# Revit family: MKH1-800-R3(R4)
name_source: partatom
category: Mechanical Equipment
revit_build: Autodesk Revit 2013 (Build: 20120221_2030(x64)
units: mm (PartAtom-declared; Revit-internal decimal feet)

## types (2) — shared parameters
Circuit breaker = 15 A
Condensation = water
Depth = 1360 mm
Description = High efficiency water cooled
Drain pipe = 18.5 mm
Height = 200 mm
Installation = Indoor installation
Liquid pipe = 19.05 mm  [stored 0.0625 ft]
Machine material = Galvanized Steel
Manufacturer = Midea
Panel color = WH101
Power supply = 220-240V ~50Hz/60Hz
Rated current = 1 A
Series = FCU
Width = 591 mm  [stored 1.93898 ft]
clearance access behind = 50 mm  [stored 0.164042 ft]
clearance access down = 90 mm
clearance access left = 150 mm
clearance access right = 150 mm
clearance access up = 1500 mm  [stored 4.92126 ft]

## per-type parameters (varying)
| type | Air Flow(H/M/L) | Cooling Capacity(H/M/L) | Heating Capacity(H/M/L) | Net Weight | Power Input(H/M/L) |
| MKH1-800-R3 | 1300/1088/782 m3/h | 7.35/6.51/5.15 kW | 8.20/7.09/5.46 kW | 31.70 kg | 123/109/83 W |
| MKH1-800-R4 | 1300/1132/836 m3/h | 8.25/7.52/5.87 kW | 8.50/7.60/5.72 kW | 34.00 kg | 118/104/82 W |

note: column(s) folded — value = type name in every type: Model

note: [stored X ft] marks values corroborated as IEEE doubles in the binary element streams (Revit-internal decimal feet)

## geometry (parser evidence)
native form markers: Sweep x5
no freeform markers — native parametric forms only
